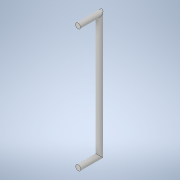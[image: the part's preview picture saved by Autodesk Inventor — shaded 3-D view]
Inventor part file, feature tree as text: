
AUTODESK INVENTOR PART (.ipt)
format: ipt  version: 2021 (Build 250183000, 183)  size: 103,424 bytes
history: native  units: mm
features: sketch x2, thicken_offset x2, plane x1, sweep x1
ambient origin geometry x8: Origin, YZ Plane, XZ Plane, XY Plane, X Axis, Y Axis, Z Axis, Center Point
bodies: Solid1 (feature_tree)
feature tree (6):
  sketch  "Sketch1"  dims[d3=0.0mm d4=0.0mm d6=25.0mm]
  plane  "Work Plane1"
  sweep  "Sweep1"
  thicken_offset  "Thicken1"
  thicken_offset  "Thicken2"
  sketch  "Sketch2"  dims[d8=25.0mm]
